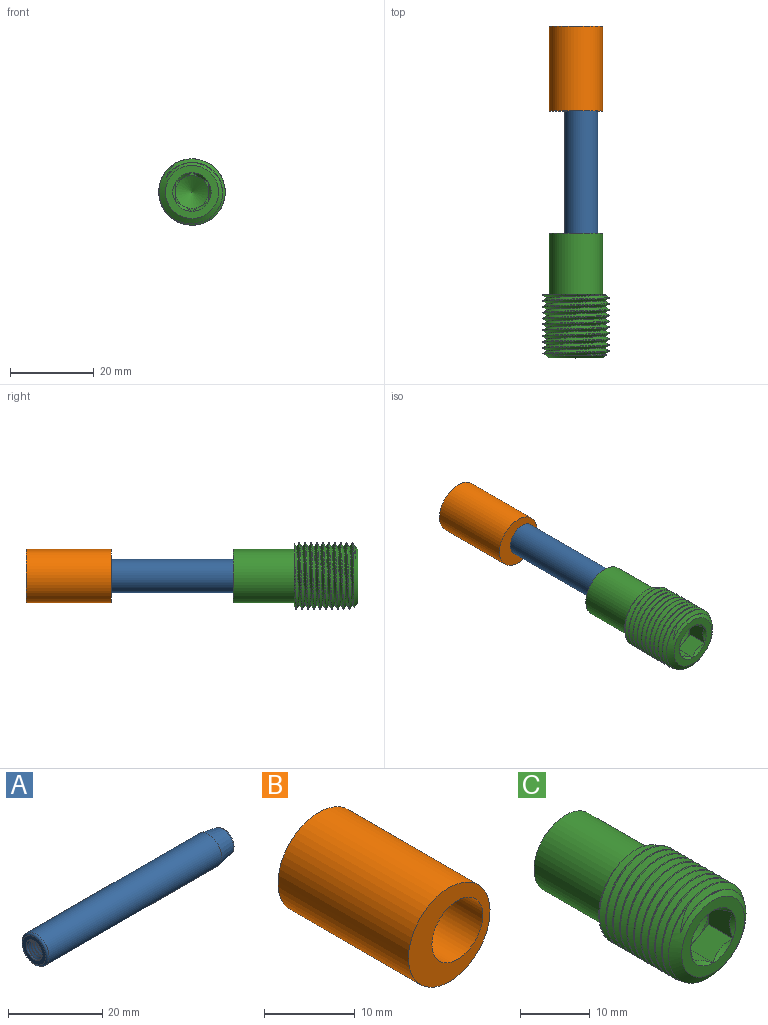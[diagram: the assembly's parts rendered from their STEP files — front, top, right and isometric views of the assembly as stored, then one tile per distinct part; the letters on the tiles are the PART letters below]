
ASSEMBLY  parts=3 mates=2
PART A: 14 faces, bbox 57.4x8.6x8.6 mm
  f0: cone r=1.62mm half-angle=60deg, axis (-1,0,0), area 9.5mm2, adj f1
  f1: cylinder r=1.62mm len=5.42mm, axis (-1,0,0), area 55.1mm2, adj f0,f2
  f2: cone r=2.41mm half-angle=60deg, axis (-1,0,0), area 7.5mm2, adj f1,f3,f10,f11,f12
  f3: cylinder r=2.41mm len=11.48mm, axis (-1,0,0), area 28.8mm2, adj f2,f4,f11,f12
  f4: plane 6.9x6.9mm, normal (-1,0,0), area 19.1mm2, adj f3,f5,f13
  f5: torus R=3.45mm, axis (-1,0,0), area 19.3mm2, adj f4,f6
  f6: cylinder r=3.97mm len=51.87mm, axis (-1,0,0), area 1293.4mm2, adj f5,f7
  f7: cone r=3.2mm half-angle=10deg, axis (-1,0,0), area 99.2mm2, adj f6,f8
  f8: torus R=2.69mm, axis (-1,0,0), area 13.7mm2, adj f7,f9
  f9: plane 5.39x5.39mm, normal (1,0,0), area 22.8mm2, adj f8
  f10: cylinder r=1.9mm len=11.26mm, axis (1,0,0), area 20.9mm2, adj f2,f11,f12,f13
  f11: bspline ~12.47x5.57mm, area 116.2mm2, adj f2,f3,f10,f13
  f12: bspline ~11.94x5.57mm, area 115.8mm2, adj f2,f3,f10,f13
  f13: cone r=2.41mm half-angle=45deg, axis (-1,0,0), area 5.1mm2, adj f4,f10,f11,f12
PART B: 4 faces, bbox 12.7x20.3x12.7 mm
  f0: cylinder r=6.35mm len=20.32mm, axis (0,-1,0), area 810.7mm2, adj f1,f3
  f1: plane 12.7x12.7mm, normal (0,1,0), area 77.2mm2, adj f0,f2
  f2: cylinder r=3.97mm len=20.32mm, axis (0,1,0), area 506.7mm2, adj f1,f3
  f3: plane 12.7x12.7mm, normal (0,-1,0), area 77.2mm2, adj f0,f2
PART C: 30 faces, bbox 17.6x31.8x17.6 mm
  f0: plane 3.44x1.98mm, normal (0,-1,0), area 0.8mm2, adj f18,f19,f24
  f1: plane 3.97x1.15mm, normal (0,-1,0), area 0.8mm2, adj f18,f23,f24
  f2: plane 3.44x1.98mm, normal (0,-1,0), area 0.8mm2, adj f22,f23,f24
  f3: plane 3.44x1.98mm, normal (0,-1,0), area 0.8mm2, adj f21,f22,f24
  f4: plane 3.97x1.15mm, normal (0,-1,0), area 0.8mm2, adj f20,f21,f24
  f5: cone r=7.94mm half-angle=55deg, axis (0,1,0), area 60.3mm2, adj f6,f7,f8,f9,f10
  f6: plane 12.7x12.7mm, normal (0,-1,0), area 60.7mm2, adj f5,f11,f12,f13,f14,f15,f16
  f7: cylinder r=7.94mm len=15.88mm, axis (0,-1,0), area 89mm2, adj f5,f8,f10,f25
  f8: bspline ~15.88x15.88mm, area 511.2mm2, adj f5,f7,f9,f25
  f9: cylinder r=7.02mm len=14.77mm, axis (0,-1,0), area 80.3mm2, adj f5,f8,f10,f25
  f10: bspline ~16.05x15.88mm, area 506.8mm2, adj f5,f7,f9,f25
  f11: cone r=4.58mm half-angle=45deg, axis (0,-1,0), area 0mm2, adj f6,f18
  f12: cone r=4.58mm half-angle=45deg, axis (0,-1,0), area 0mm2, adj f6,f19
  f13: cone r=4.58mm half-angle=45deg, axis (0,-1,0), area 0mm2, adj f6,f20
  f14: cone r=4.58mm half-angle=45deg, axis (0,-1,0), area 0mm2, adj f6,f21
  f15: cone r=4.58mm half-angle=45deg, axis (0,-1,0), area 0mm2, adj f6,f22
  f16: cone r=4.58mm half-angle=45deg, axis (0,-1,0), area 0mm2, adj f6,f23
  f17: plane 3.44x1.98mm, normal (0,-1,0), area 0.8mm2, adj f19,f20,f24
  f18: plane 6.7x5.71mm, normal (0.5,0,-0.87), area 20.9mm2, adj f0,f1,f11,f19,f23
  f19: plane 6.7x6.33mm, normal (1,0,0), area 20.9mm2, adj f0,f12,f17,f18,f20
  f20: plane 6.7x5.71mm, normal (0.5,0,0.87), area 20.9mm2, adj f4,f13,f17,f19,f21
  f21: plane 6.7x5.71mm, normal (-0.5,0,0.87), area 20.9mm2, adj f3,f4,f14,f20,f22
  f22: plane 6.7x6.33mm, normal (-1,0,0), area 20.9mm2, adj f2,f3,f15,f21,f23
  f23: plane 6.7x5.71mm, normal (-0.5,0,-0.87), area 20.9mm2, adj f1,f2,f16,f18,f22
  f24: cone r=3.97mm half-angle=60deg, axis (0,-1,0), area 57.1mm2, adj f0,f1,f2,f3,f4,f17
  f25: plane 15.56x15.55mm, normal (0,1,0), area 49.4mm2, adj f7,f8,f9,f10,f26
  f26: cylinder r=6.35mm len=14.61mm, axis (0,-1,0), area 582.7mm2, adj f25,f27
  f27: plane 12.7x12.7mm, normal (0,1,0), area 77.2mm2, adj f26,f29
  f28: cone r=0mm half-angle=59deg, axis (0,1,0), area 57.7mm2, adj f29
  f29: cylinder r=3.97mm len=17.78mm, axis (0,1,0), area 443.4mm2, adj f27,f28
PLACE A rot(axis=(0.58,0.58,0.58),120deg) t=(3.28,4.72,2.01)mm
PLACE B t=(2.01,15.48,2.01)mm
PLACE C t=(2.01,-10.56,2.01)mm fixed
MATE fastened A.f0 <-> C.f28  axis (0,-1,0) through (3.28,-23.86,2.01)mm
MATE fastened B.f2 <-> C.f28  axis (0,-1,0) through (3.28,18.05,2.01)mm
